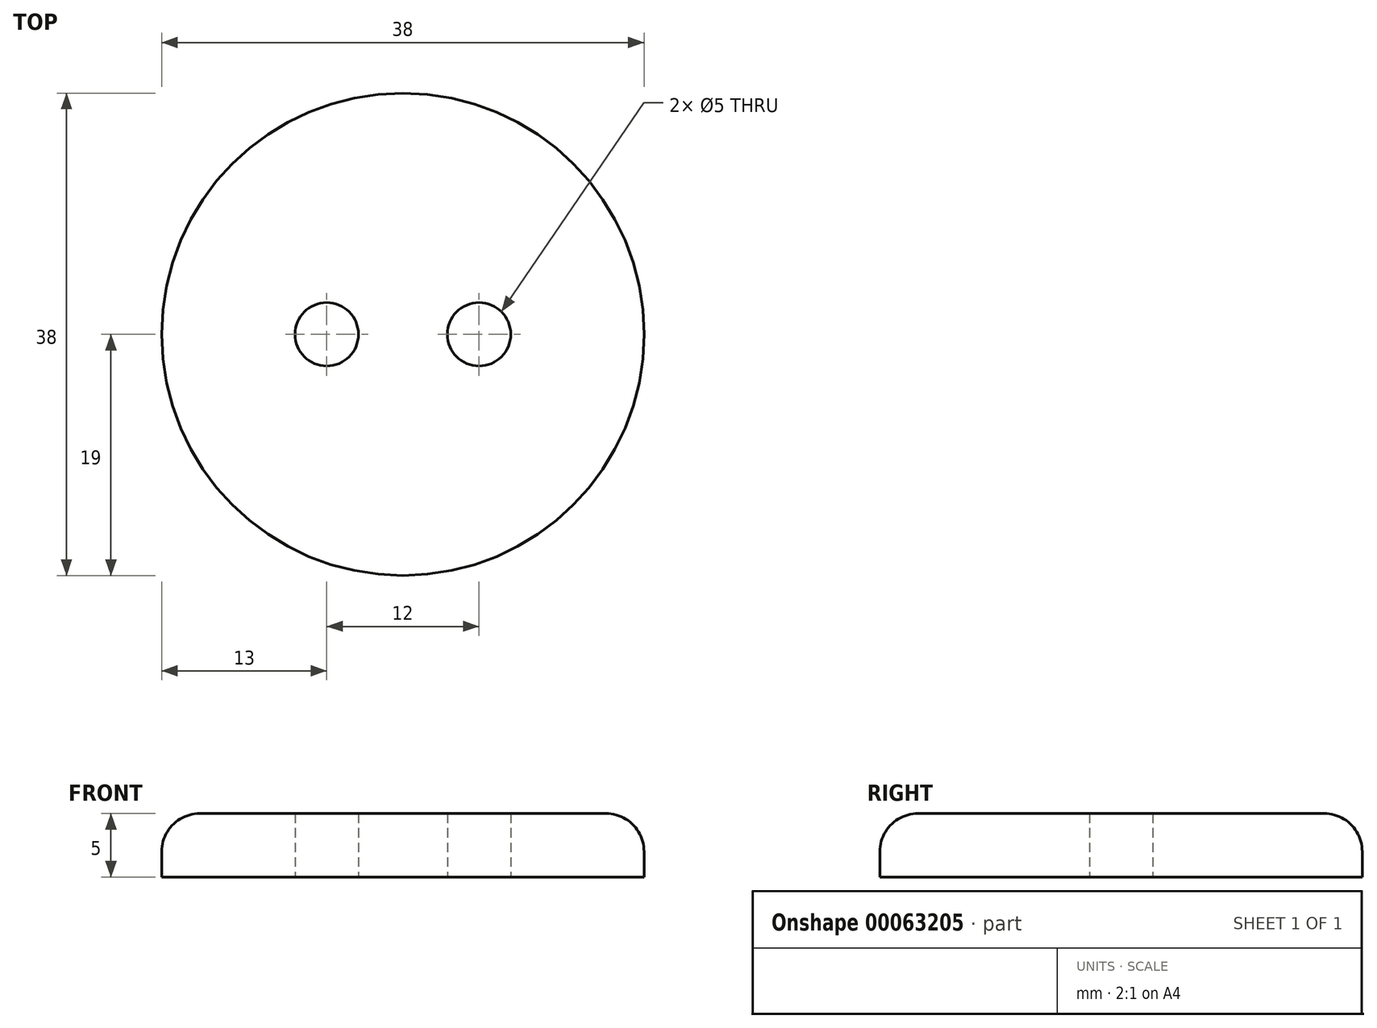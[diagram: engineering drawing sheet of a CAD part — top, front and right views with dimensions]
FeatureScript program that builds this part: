
annotation { "Feature Type Name" : "Feature", "Feature Type Description" : "" }
export const myFeature = defineFeature(function(context is Context, id is Id, definition is map)
    precondition{}
    {
        {
            var Q0;
            Q0=qCreatedBy(makeId("Top.planeOp"),FACE);
            var sketch = newSketch(context, id + "F0", { "sketchPlane" : qUnion([Q0])});
            skCircle(sketch, "E0", {"center": v(0, 0) * mm, "radius": 19 * mm});
            skCircle(sketch, "E1", {"center": v(-6, 0) * mm, "radius": 2.5 * mm});
            skCircle(sketch, "E2", {"center": v(6, 0) * mm, "radius": 2.5 * mm});
            skSolve(sketch);
        }
        {
            var Q0;
            Q0=makeQuery(id+"F0.imprint","IMPRINT",FACE,{"disambiguationData":[TD([[makeQuery(id+"F0.imprint","IMPRINT",EDGE,{"derivedFrom":sQuery(id+"F0.wireOp",EDGE,"E0")}),1.0]])]});
            extrude(context, id + "F1", {"entities" : qUnion([Q0]), "depth" : 5 * mm, "offsetDistance" : 25 * mm});
        }
        {
            var Q0;
            Q0=makeQuery(id+"F1.opExtrude","CAP_EDGE",EDGE,{"disambiguationData":[OSD([sQuery(id+"F0.wireOp",EDGE,"E0")])],"isStart":false});
            fillet(context, id + "F2", {"entities" : qUnion([Q0]), "radius" : 3 * mm, "tangentPropagation" : true, "allowEdgeOverflow" : false});
        }
    });
